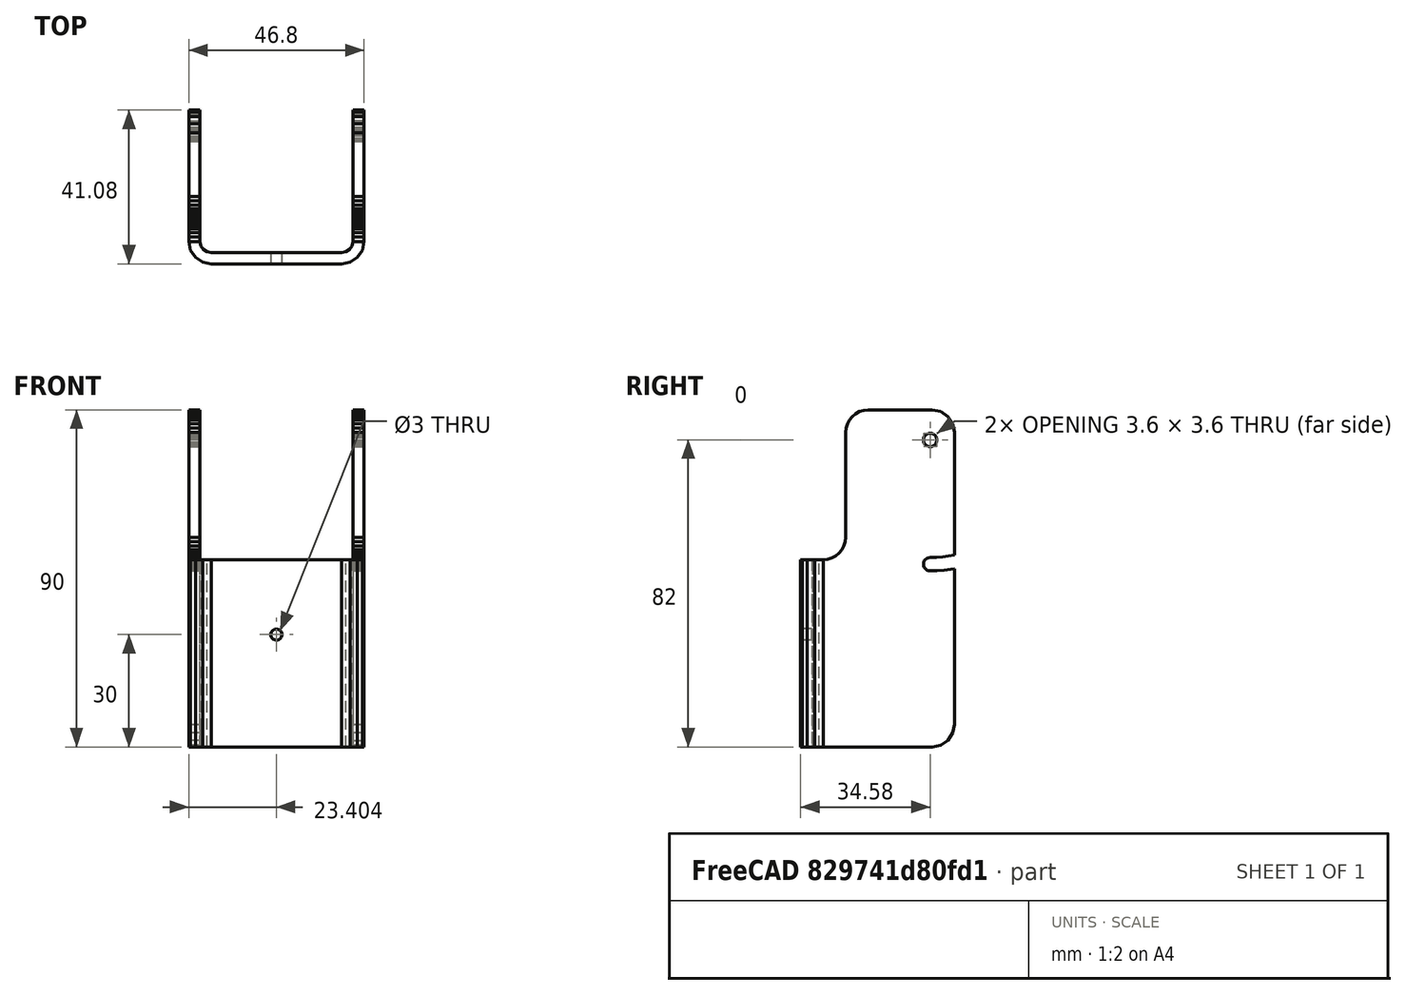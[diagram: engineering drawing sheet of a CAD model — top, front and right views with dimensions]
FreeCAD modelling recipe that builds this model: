
FCSTD DOCUMENT  (FreeCAD 0.20R29177 (Git))
Label: Acrylic Shield
License: All rights reserved
LicenseURL: http://en.wikipedia.org/wiki/All_rights_reserved
objects: App::DocumentObjectGroup×3, Part::Feature×2, PartDesign::CoordinateSystem×2, App::Part×2, Mesh::Feature×1, Part::Refine×1, PartDesign::FeatureBase×1, App::FeaturePython×1, Sketcher::SketchObject×1, PartDesign::Pocket×1, PartDesign::Body×1
note: 10 computed .brp shape members not serialized (recipe doc carries the construction recipe); baked Part::Feature solids carry a one-line shape summary decoded from their .brp

FEATURE [Mesh::Feature] Acrylic_Shield  label="Acrylic Shield"
FEATURE [Part::Feature] Acrylic_Shield001
  shape: bbox 46.8 x 41.08 x 90 mm, 660 faces, 0 solids (baked)
FEATURE [Part::Feature] Acrylic_Shield001_solid  label="Acrylic_Shield001 (Solid)"
  shape: bbox 46.8 x 41.08 x 90 mm, 660 faces (baked)
FEATURE [Part::Refine] Acrylic_Shield001_solid001  label="Acrylic_Shield001 (Solid)001"
  Source = -> Acrylic_Shield001_solid
FEATURE [PartDesign::FeatureBase] BaseFeature
  BaseFeature = -> Acrylic_Shield001_solid001
FEATURE [PartDesign::CoordinateSystem] LCS_0
  AttacherType = Attacher::AttachEngine3D
  MapMode = 2
  Support = -> [X_Axis001]
FEATURE [PartDesign::CoordinateSystem] LCS_Origin
  AttacherType = Attacher::AttachEngine3D
  MapMode = 2
  Support = -> [X_Axis002]
FEATURE [App::FeaturePython] Variables  # WARN: FeaturePython — macro-defined, semantics opaque (R4)
  Type = App::PropertyContainer
FEATURE [App::DocumentObjectGroup] Constraints
FEATURE [App::DocumentObjectGroup] Configurations
FEATURE [App::Part] Assembly
  AssemblyType = Part::Link
  Group = -> [LCS_Origin,Variables,Constraints,Configurations]
  Origin = -> Origin002
  Type = Assembly
FEATURE [Sketcher::SketchObject] Sketch
  ExternalGeometry = -> [BaseFeature]
  FullyConstrained = true
  MapMode = 5
  Placement = pos=(0,2.68986e-08,0) rot=(1,0,0;1.5708rad)
  Support = -> [BaseFeature]
  sketch-geometry (2):
    g0: Circle CenterX=30.1441 CenterY=30 CenterZ=0 NormalX=0 NormalY=0 NormalZ=1 AngleXU=0 Radius=1.5
    g1: LineSegment StartX=30.1441 StartY=30 StartZ=0 EndX=30.1441 EndY=50 EndZ=0
  constraints (5):
    c: Coincident(g1,g0)
    c: Symmetric(g-3,g-3,g1)
    c: Vertical(g1)
    c: DistanceY(g1,g1) = 20
    c: Diameter(g0) = 3
FEATURE [PartDesign::Pocket] Pocket
  BaseFeature = -> BaseFeature
  Direction = (0,1,9.70576e-10)
  Length = 0
  Length2 = 5
  Profile = -> Sketch
  ReferenceAxis = -> Sketch [N_Axis]
  Type = 3
  UpToFace = -> BaseFeature [Face141]
FEATURE [PartDesign::Body] Body
  BaseFeature = -> Acrylic_Shield001_solid001
  Group = -> [BaseFeature,Sketch,Pocket]
  Origin = -> Origin
  Placement = pos=(-30,0,0) rot=(0,0,1;0rad)
  Tip = -> Pocket
FEATURE [App::Part] Acrylic_Shield002
  Group = -> [LCS_0,Acrylic_Shield001_solid,Body,Acrylic_Shield001_solid001,Acrylic_Shield]
  LabelDocUser = Acrylic Shield
  LabelPartUser = Acrylic_Shield002
  Origin = -> Origin001
  ShapeVolumeUser = 90.0 mm x 41.08 mm x 46.8 mm
FEATURE [App::DocumentObjectGroup] Parts
  Group = -> [Acrylic_Shield002]
